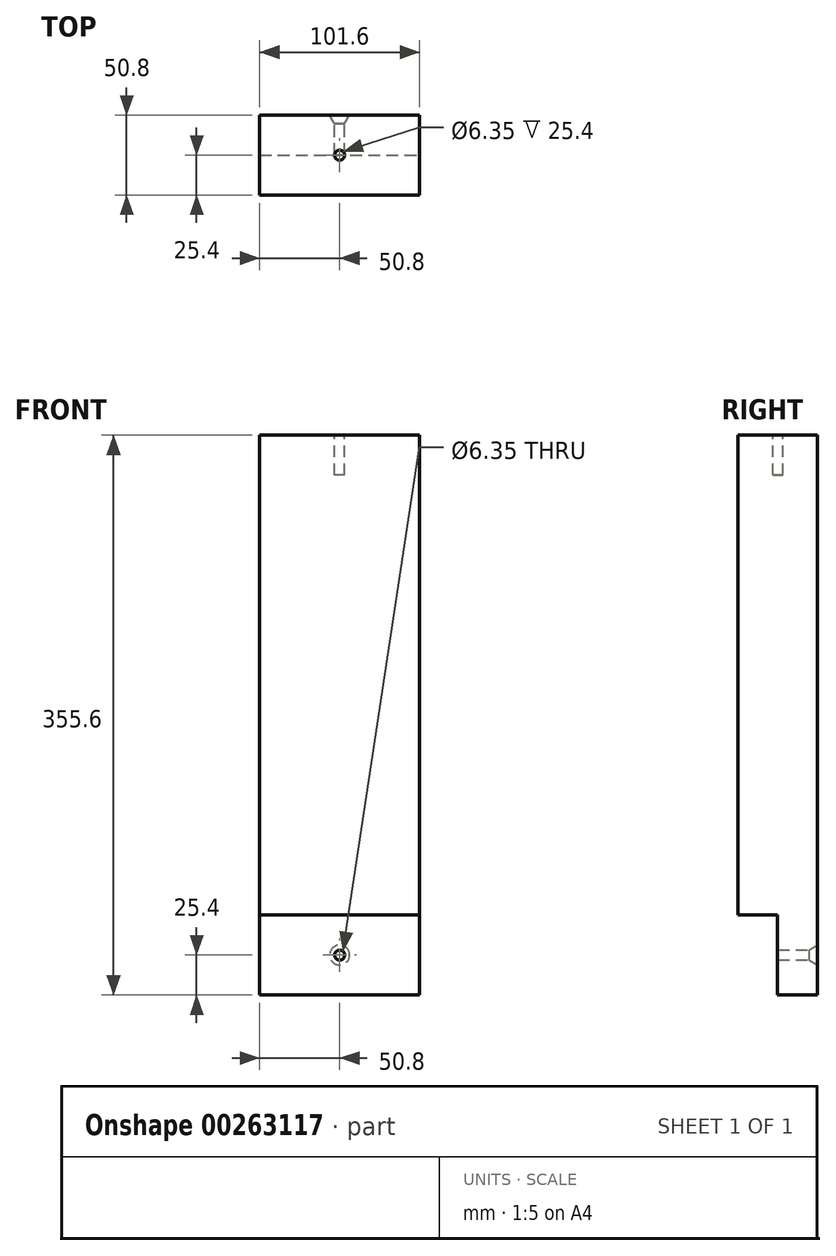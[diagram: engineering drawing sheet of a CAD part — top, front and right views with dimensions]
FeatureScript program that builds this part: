
annotation { "Feature Type Name" : "Feature", "Feature Type Description" : "" }
export const myFeature = defineFeature(function(context is Context, id is Id, definition is map)
    precondition{}
    {
        {
            var Q0;
            Q0=qCreatedBy(makeId("Top.planeOp"),FACE);
            var sketch = newSketch(context, id + "F0", { "sketchPlane" : qUnion([Q0])});
            skLineSegment(sketch, "E0.bottom", {"start": v(50.8, 25.4) * mm, "end": v(-50.8, 25.4) * mm});
            skLineSegment(sketch, "E0.top", {"start": v(50.8, -25.4) * mm, "end": v(-50.8, -25.4) * mm});
            skLineSegment(sketch, "E0.left", {"start": v(50.8, 25.4) * mm, "end": v(50.8, -25.4) * mm});
            skLineSegment(sketch, "E0.right", {"start": v(-50.8, 25.4) * mm, "end": v(-50.8, -25.4) * mm});
            skPoint(sketch, "E0.middle", {"position": v(0, 0) * mm});
            skSolve(sketch);
        }
        {
            var Q0;
            Q0=qSketchRegion(id+"F0",true);
            extrude(context, id + "F1", {"entities" : qUnion([Q0]), "depth" : 355.6 * mm});
        }
        {
            var Q0;
            Q0=makeQuery(id+"F1.opExtrude","CAP_FACE",FACE,{"disambiguationData":[OSD([sQuery(id+"F0.wireOp",EDGE,"E0.bottom"),sQuery(id+"F0.wireOp",EDGE,"E0.top"),sQuery(id+"F0.wireOp",EDGE,"E0.left"),sQuery(id+"F0.wireOp",EDGE,"E0.right")])],"isStart":true});
            var sketch = newSketch(context, id + "F2", { "sketchPlane" : qUnion([Q0])});
            skLineSegment(sketch, "E1.bottom", {"start": v(-50.8, 25.4) * mm, "end": v(50.8, 25.4) * mm});
            skLineSegment(sketch, "E1.top", {"start": v(-50.8, 0) * mm, "end": v(50.8, 0) * mm});
            skLineSegment(sketch, "E1.left", {"start": v(-50.8, 25.4) * mm, "end": v(-50.8, 0) * mm});
            skLineSegment(sketch, "E1.right", {"start": v(50.8, 25.4) * mm, "end": v(50.8, 0) * mm});
            skSolve(sketch);
        }
        {
            var Q0;
            Q0=qSketchRegion(id+"F2",true);
            extrude(context, id + "F3", {"entities" : qUnion([Q0]), "operationType" : NewBodyOperationType.REMOVE, "oppositeDirection" : true, "depth" : 50.8 * mm});
        }
        {
            var Q0;
            Q0=makeQuery(id+"F1.opExtrude","SWEPT_FACE",FACE,{"disambiguationData":[OSD([sQuery(id+"F0.wireOp",EDGE,"E0.bottom")])]});
            var sketch = newSketch(context, id + "F4", { "sketchPlane" : qUnion([Q0])});
            skPoint(sketch, "E2.centerSnap0", {"position": v(0, 355.6) * mm});
            skCircle(sketch, "E3", {"center": v(0, 25.4) * mm, "radius": 3.18 * mm});
            skPoint(sketch, "E2.center.orphan", {"position": v(0, 330.2) * mm});
            skSolve(sketch);
        }
        {
            var Q0;
            Q0=qSketchRegion(id+"F4",true);
            extrude(context, id + "F5", {"entities" : qUnion([Q0]), "operationType" : NewBodyOperationType.REMOVE, "endBound" : BoundingType.THROUGH_ALL, "oppositeDirection" : true, "depth" : 25.4 * mm});
        }
        {
            var Q0;
            Q0=makeQuery(id+"F1.opExtrude","CAP_FACE",FACE,{"disambiguationData":[OSD([sQuery(id+"F0.wireOp",EDGE,"E0.bottom"),sQuery(id+"F0.wireOp",EDGE,"E0.top"),sQuery(id+"F0.wireOp",EDGE,"E0.left"),sQuery(id+"F0.wireOp",EDGE,"E0.right")])],"isStart":false});
            var sketch = newSketch(context, id + "F6", { "sketchPlane" : qUnion([Q0])});
            skCircle(sketch, "E4", {"center": v(0, 0) * mm, "radius": 3.18 * mm});
            skSolve(sketch);
        }
        {
            var Q0;
            Q0 = qSketchRegion(id + "F6", true);
            extrude(context, id + "F7", {"entities" : qUnion([Q0]), "operationType" : NewBodyOperationType.REMOVE, "oppositeDirection" : true, "depth" : 25.4 * mm});
        }
        {
            var Q0;
            Q0=makeQuery(id+"F1.opExtrude","SWEPT_FACE",FACE,{"disambiguationData":[OSD([sQuery(id+"F0.wireOp",EDGE,"E0.bottom")])]});
            var sketch = newSketch(context, id + "F8", { "sketchPlane" : qUnion([Q0])});
            skCircle(sketch, "E5", {"center": v(0, 25.4) * mm, "radius": 6.35 * mm});
            skSolve(sketch);
        }
        {
            var Q0;
            Q0 = qSketchRegion(id + "F8", true);
            extrude(context, id + "F9", {"entities" : qUnion([Q0]), "operationType" : NewBodyOperationType.REMOVE, "oppositeDirection" : true, "depth" : 6.35 * mm, "hasDraft" : true, "draftAngle" : 30 * degree, "draftPullDirection" : true});
        }
    });
